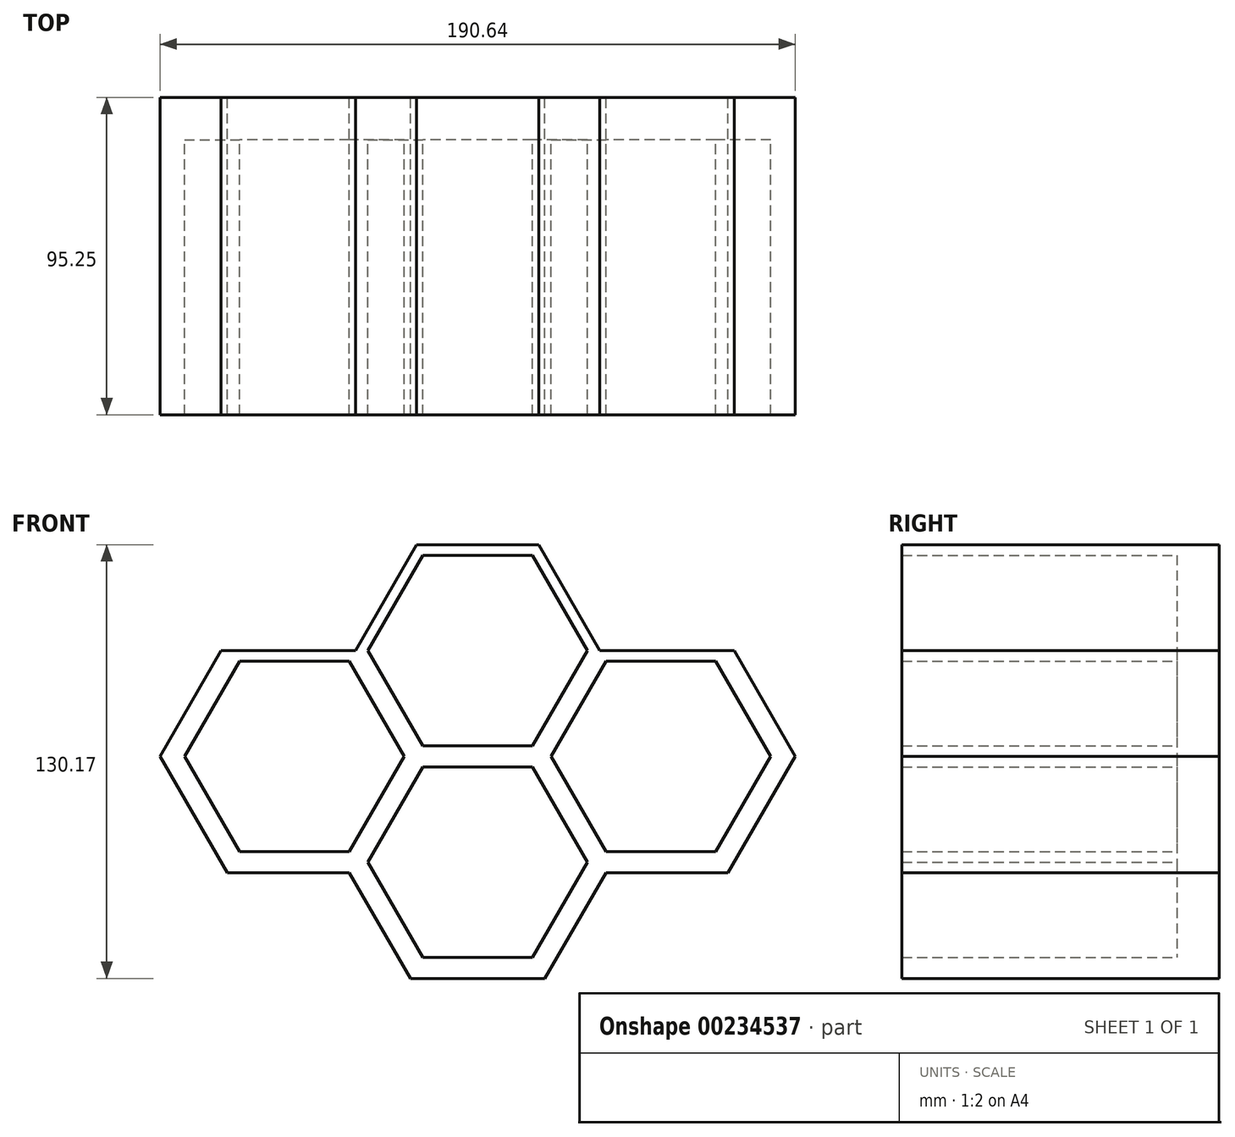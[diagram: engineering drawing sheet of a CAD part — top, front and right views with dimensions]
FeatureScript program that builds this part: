
annotation { "Feature Type Name" : "Feature", "Feature Type Description" : "" }
export const myFeature = defineFeature(function(context is Context, id is Id, definition is map)
    precondition{}
    {
        {
            var Q0;
            Q0=qCreatedBy(makeId("Front.planeOp"),FACE);
            var sketch = newSketch(context, id + "F0", { "sketchPlane" : qUnion([Q0])});
            skLineSegment(sketch, "E0.3", {"start": v(105.7, 35.04) * mm, "end": v(87.38, 3.3) * mm});
            skLineSegment(sketch, "E0.4", {"start": v(87.38, 3.3) * mm, "end": v(50.71, 3.3) * mm});
            skCircle(sketch, "E1.cCircle", {"center": v(69.05, -28.46) * mm, "radius": 28.57 * mm, "construction": true});
            skLineSegment(sketch, "E1.0", {"start": v(36.05, -28.46) * mm, "end": v(52.55, 0.12) * mm});
            skLineSegment(sketch, "E1.1", {"start": v(52.55, 0.12) * mm, "end": v(85.54, 0.12) * mm});
            skLineSegment(sketch, "E1.2", {"start": v(85.54, 0.12) * mm, "end": v(102.04, -28.46) * mm});
            skLineSegment(sketch, "E1.3", {"start": v(102.04, -28.46) * mm, "end": v(85.54, -57.03) * mm});
            skLineSegment(sketch, "E1.4", {"start": v(85.54, -57.03) * mm, "end": v(52.55, -57.03) * mm});
            skLineSegment(sketch, "E1.5", {"start": v(52.55, -57.03) * mm, "end": v(36.05, -28.46) * mm});
            skPoint(sketch, "E1.0.midPoint", {"position": v(44.3, -14.17) * mm});
            skCircle(sketch, "E2.cCircle", {"center": v(69.05, -28.46) * mm, "radius": 31.75 * mm, "construction": true});
            skLineSegment(sketch, "E2.0", {"start": v(32.38, -28.46) * mm, "end": v(50.71, 3.3) * mm});
            skLineSegment(sketch, "E2.1", {"start": v(50.71, 3.3) * mm, "end": v(87.38, 3.3) * mm});
            skLineSegment(sketch, "E2.2", {"start": v(87.38, 3.3) * mm, "end": v(105.7, -28.46) * mm});
            skLineSegment(sketch, "E2.3", {"start": v(105.7, -28.46) * mm, "end": v(87.38, -60.2) * mm});
            skLineSegment(sketch, "E2.4", {"start": v(87.38, -60.2) * mm, "end": v(50.71, -60.2) * mm});
            skLineSegment(sketch, "E2.5", {"start": v(50.71, -60.2) * mm, "end": v(32.38, -28.46) * mm});
            skPoint(sketch, "E2.0.midPoint", {"position": v(41.55, -12.58) * mm});
            skCircle(sketch, "E3.cCircle", {"center": v(124.04, 3.3) * mm, "radius": 28.58 * mm, "construction": true});
            skLineSegment(sketch, "E3.0", {"start": v(91.04, 3.3) * mm, "end": v(107.54, 31.87) * mm});
            skLineSegment(sketch, "E3.1", {"start": v(107.54, 31.87) * mm, "end": v(140.54, 31.87) * mm});
            skLineSegment(sketch, "E3.2", {"start": v(140.54, 31.87) * mm, "end": v(157.03, 3.3) * mm});
            skLineSegment(sketch, "E3.3", {"start": v(157.03, 3.3) * mm, "end": v(140.54, -25.28) * mm});
            skLineSegment(sketch, "E3.4", {"start": v(140.54, -25.28) * mm, "end": v(107.54, -25.28) * mm});
            skLineSegment(sketch, "E3.5", {"start": v(107.54, -25.28) * mm, "end": v(91.04, 3.3) * mm});
            skPoint(sketch, "E3.0.midPoint", {"position": v(99.3, 17.58) * mm});
            skCircle(sketch, "E4.cCircle", {"center": v(124.04, 3.3) * mm, "radius": 31.75 * mm, "construction": true});
            skLineSegment(sketch, "E4.0", {"start": v(87.38, 3.3) * mm, "end": v(105.7, 35.04) * mm});
            skLineSegment(sketch, "E4.1", {"start": v(105.7, 35.04) * mm, "end": v(142.37, 35.04) * mm});
            skLineSegment(sketch, "E4.2", {"start": v(142.37, 35.04) * mm, "end": v(160.7, 3.3) * mm});
            skLineSegment(sketch, "E4.3", {"start": v(160.7, 3.3) * mm, "end": v(142.37, -28.46) * mm});
            skLineSegment(sketch, "E4.4", {"start": v(142.37, -28.46) * mm, "end": v(105.7, -28.46) * mm});
            skLineSegment(sketch, "E4.5", {"start": v(105.7, -28.46) * mm, "end": v(87.38, 3.3) * mm});
            skPoint(sketch, "E4.0.midPoint", {"position": v(96.54, 19.17) * mm});
            skLineSegment(sketch, "E5.4", {"start": v(142.37, 35.04) * mm, "end": v(105.7, 35.04) * mm});
            skCircle(sketch, "E6.cCircle", {"center": v(124.04, -60.2) * mm, "radius": 28.58 * mm, "construction": true});
            skLineSegment(sketch, "E6.0", {"start": v(91.04, -60.2) * mm, "end": v(107.54, -31.63) * mm});
            skLineSegment(sketch, "E6.1", {"start": v(107.54, -31.63) * mm, "end": v(140.54, -31.63) * mm});
            skLineSegment(sketch, "E6.2", {"start": v(140.54, -31.63) * mm, "end": v(157.03, -60.2) * mm});
            skLineSegment(sketch, "E6.3", {"start": v(157.03, -60.2) * mm, "end": v(140.54, -88.78) * mm});
            skLineSegment(sketch, "E6.4", {"start": v(140.54, -88.78) * mm, "end": v(107.54, -88.78) * mm});
            skLineSegment(sketch, "E6.5", {"start": v(107.54, -88.78) * mm, "end": v(91.04, -60.2) * mm});
            skPoint(sketch, "E6.0.midPoint", {"position": v(99.3, -45.92) * mm});
            skCircle(sketch, "E7.cCircle", {"center": v(124.04, -60.2) * mm, "radius": 31.75 * mm, "construction": true});
            skLineSegment(sketch, "E7.0", {"start": v(87.38, -60.2) * mm, "end": v(105.7, -28.46) * mm});
            skLineSegment(sketch, "E7.1", {"start": v(105.7, -28.46) * mm, "end": v(142.37, -28.46) * mm});
            skLineSegment(sketch, "E7.2", {"start": v(142.37, -28.46) * mm, "end": v(160.7, -60.2) * mm});
            skLineSegment(sketch, "E7.3", {"start": v(160.7, -60.2) * mm, "end": v(142.37, -91.96) * mm});
            skLineSegment(sketch, "E7.4", {"start": v(142.37, -91.96) * mm, "end": v(105.7, -91.96) * mm});
            skLineSegment(sketch, "E7.5", {"start": v(105.7, -91.96) * mm, "end": v(87.38, -60.2) * mm});
            skPoint(sketch, "E7.0.midPoint", {"position": v(96.54, -44.33) * mm});
            skCircle(sketch, "E8.cCircle", {"center": v(179.03, -28.46) * mm, "radius": 28.57 * mm, "construction": true});
            skLineSegment(sketch, "E8.0", {"start": v(146.03, -28.46) * mm, "end": v(162.53, 0.12) * mm});
            skLineSegment(sketch, "E8.1", {"start": v(162.53, 0.12) * mm, "end": v(195.53, 0.12) * mm});
            skLineSegment(sketch, "E8.2", {"start": v(195.53, 0.12) * mm, "end": v(212.03, -28.46) * mm});
            skLineSegment(sketch, "E8.3", {"start": v(212.03, -28.46) * mm, "end": v(195.53, -57.03) * mm});
            skLineSegment(sketch, "E8.4", {"start": v(195.53, -57.03) * mm, "end": v(162.53, -57.03) * mm});
            skLineSegment(sketch, "E8.5", {"start": v(162.53, -57.03) * mm, "end": v(146.03, -28.46) * mm});
            skPoint(sketch, "E8.0.midPoint", {"position": v(154.28, -14.17) * mm});
            skCircle(sketch, "E9.cCircle", {"center": v(179.03, -28.46) * mm, "radius": 31.75 * mm, "construction": true});
            skLineSegment(sketch, "E9.0", {"start": v(142.37, -28.46) * mm, "end": v(160.7, 3.3) * mm});
            skLineSegment(sketch, "E9.1", {"start": v(160.7, 3.3) * mm, "end": v(197.36, 3.3) * mm});
            skLineSegment(sketch, "E9.2", {"start": v(197.36, 3.3) * mm, "end": v(215.7, -28.46) * mm});
            skLineSegment(sketch, "E9.3", {"start": v(215.7, -28.46) * mm, "end": v(197.36, -60.2) * mm});
            skLineSegment(sketch, "E9.4", {"start": v(197.36, -60.2) * mm, "end": v(160.7, -60.2) * mm});
            skLineSegment(sketch, "E9.5", {"start": v(160.7, -60.2) * mm, "end": v(142.37, -28.46) * mm});
            skPoint(sketch, "E9.0.midPoint", {"position": v(151.53, -12.58) * mm});
            skLineSegment(sketch, "E10.4", {"start": v(197.36, 3.3) * mm, "end": v(160.7, 3.3) * mm});
            skLineSegment(sketch, "E10.5", {"start": v(160.7, 3.3) * mm, "end": v(142.37, 35.04) * mm});
            skLineSegment(sketch, "E11", {"start": v(47.05, 3.3) * mm, "end": v(28.72, -28.46) * mm});
            skLineSegment(sketch, "E12", {"start": v(28.72, -28.46) * mm, "end": v(48.88, -63.38) * mm});
            skLineSegment(sketch, "E13", {"start": v(48.88, -63.38) * mm, "end": v(85.54, -63.38) * mm});
            skLineSegment(sketch, "E14", {"start": v(85.54, -63.38) * mm, "end": v(103.87, -95.13) * mm});
            skLineSegment(sketch, "E15", {"start": v(103.87, -95.13) * mm, "end": v(144.2, -95.13) * mm});
            skLineSegment(sketch, "E16", {"start": v(144.2, -95.13) * mm, "end": v(162.53, -63.38) * mm});
            skLineSegment(sketch, "E17", {"start": v(162.53, -63.38) * mm, "end": v(199.2, -63.38) * mm});
            skLineSegment(sketch, "E18", {"start": v(199.2, -63.38) * mm, "end": v(219.36, -28.46) * mm});
            skLineSegment(sketch, "E19", {"start": v(219.36, -28.46) * mm, "end": v(201.03, 3.3) * mm});
            skLineSegment(sketch, "E20", {"start": v(50.71, 3.3) * mm, "end": v(47.05, 3.3) * mm});
            skLineSegment(sketch, "E21", {"start": v(201.03, 3.3) * mm, "end": v(197.36, 3.3) * mm});
            skSolve(sketch);
        }
        {
            var Q0;
            Q0=makeQuery(id+"F0.imprint","IMPRINT",FACE,{"disambiguationData":[TD([[makeQuery(id+"F0.imprint","IMPRINT",EDGE,{"derivedFrom":sQuery(id+"F0.wireOp",EDGE,"68d16a58-0471-4e1c-b2b3-2a61df7c0d9d.0")}),-1.0]])]});
            var Q1;
            Q1=makeQuery(id+"F0.imprint","IMPRINT",FACE,{"disambiguationData":[TD([[makeQuery(id+"F0.imprint","IMPRINT",EDGE,{"derivedFrom":sQuery(id+"F0.wireOp",EDGE,"E8.0")}),-1.0]])]});
            var Q2;
            Q2=makeQuery(id+"F0.imprint","IMPRINT",FACE,{"disambiguationData":[TD([[makeQuery(id+"F0.imprint","IMPRINT",EDGE,{"derivedFrom":sQuery(id+"F0.wireOp",EDGE,"cad1e4f3-bd43-45ec-b31a-1d5006939c94.0")}),-1.0]])]});
            var Q3;
            Q3=makeQuery(id+"F0.imprint","IMPRINT",FACE,{"disambiguationData":[TD([[makeQuery(id+"F0.imprint","IMPRINT",EDGE,{"derivedFrom":sQuery(id+"F0.wireOp",EDGE,"b43d4d8c-f78a-4ff8-8565-99a66ce6ec5f.0")}),-1.0]])]});
            var Q4;
            Q4=makeQuery(id+"F0.imprint","IMPRINT",FACE,{"disambiguationData":[TD([[makeQuery(id+"F0.imprint","IMPRINT",EDGE,{"derivedFrom":sQuery(id+"F0.wireOp",EDGE,"8c75d941-d110-4871-aa41-90a72d60fb2b.0")}),-1.0]])]});
            var Q5;
            Q5=makeQuery(id+"F0.imprint","IMPRINT",FACE,{"disambiguationData":[TD([[makeQuery(id+"F0.imprint","IMPRINT",EDGE,{"derivedFrom":sQuery(id+"F0.wireOp",EDGE,"258573fa-3544-418e-8bc5-5d37e5b8ba09.0")}),-1.0]])]});
            var Q6;
            Q6=makeQuery(id+"F0.imprint","IMPRINT",FACE,{"disambiguationData":[TD([[makeQuery(id+"F0.imprint","IMPRINT",EDGE,{"derivedFrom":sQuery(id+"F0.wireOp",EDGE,"0bf0733b-7d93-4c2e-8366-56d2cde24658.0")}),-1.0]])]});
            var Q7;
            Q7=makeQuery(id+"F0.imprint","IMPRINT",FACE,{"disambiguationData":[TD([[makeQuery(id+"F0.imprint","IMPRINT",EDGE,{"derivedFrom":sQuery(id+"F0.wireOp",EDGE,"93717492-86db-456f-ae55-f71e4e93837b.0")}),-1.0]])]});
            var Q8;
            Q8=makeQuery(id+"F0.imprint","IMPRINT",FACE,{"disambiguationData":[TD([[makeQuery(id+"F0.imprint","IMPRINT",EDGE,{"derivedFrom":sQuery(id+"F0.wireOp",EDGE,"f16ea8c9-6b67-4651-8441-f7eb3c0ce7d7.0")}),-1.0]])]});
            var Q9;
            Q9=makeQuery(id+"F0.imprint","IMPRINT",FACE,{"disambiguationData":[TD([[makeQuery(id+"F0.imprint","IMPRINT",EDGE,{"derivedFrom":sQuery(id+"F0.wireOp",EDGE,"0306a0a6-7289-4661-a415-5fa5585f2cb5.0")}),-1.0]])]});
            var Q10;
            Q10=makeQuery(id+"F0.imprint","IMPRINT",FACE,{"disambiguationData":[TD([[makeQuery(id+"F0.imprint","IMPRINT",EDGE,{"derivedFrom":sQuery(id+"F0.wireOp",EDGE,"0a91a14e-ea0c-483f-91eb-c48bd73cb0e6.0")}),-1.0]])]});
            var Q11;
            Q11=makeQuery(id+"F0.imprint","IMPRINT",FACE,{"disambiguationData":[TD([[makeQuery(id+"F0.imprint","IMPRINT",EDGE,{"derivedFrom":sQuery(id+"F0.wireOp",EDGE,"cbfd9497-f7fe-4f18-9288-d90aa8075d81.0")}),-1.0]])]});
            var Q12;
            Q12=makeQuery(id+"F0.imprint","IMPRINT",FACE,{"disambiguationData":[TD([[makeQuery(id+"F0.imprint","IMPRINT",EDGE,{"derivedFrom":sQuery(id+"F0.wireOp",EDGE,"6282d196-dd8f-4bb0-bca4-b9108e277473.0")}),-1.0]])]});
            var Q13;
            Q13=makeQuery(id+"F0.imprint","IMPRINT",FACE,{"disambiguationData":[TD([[makeQuery(id+"F0.imprint","IMPRINT",EDGE,{"derivedFrom":sQuery(id+"F0.wireOp",EDGE,"084ca30c-4dc0-463f-bfd9-557787ed9a2f.0")}),-1.0]])]});
            var Q14;
            Q14=makeQuery(id+"F0.imprint","IMPRINT",FACE,{"disambiguationData":[TD([[makeQuery(id+"F0.imprint","IMPRINT",EDGE,{"derivedFrom":sQuery(id+"F0.wireOp",EDGE,"06c29831-6b25-410b-9247-4ee044b7735c.0")}),-1.0]])]});
            var Q15;
            Q15=makeQuery(id+"F0.imprint","IMPRINT",FACE,{"disambiguationData":[TD([[makeQuery(id+"F0.imprint","IMPRINT",EDGE,{"derivedFrom":sQuery(id+"F0.wireOp",EDGE,"b8eec94e-d97e-439b-aaac-63499233db4c.0")}),-1.0]])]});
            var Q16;
            Q16=makeQuery(id+"F0.imprint","IMPRINT",FACE,{"disambiguationData":[TD([[makeQuery(id+"F0.imprint","IMPRINT",EDGE,{"derivedFrom":sQuery(id+"F0.wireOp",EDGE,"E1.0")}),-1.0]])]});
            var Q17;
            Q17=makeQuery(id+"F0.imprint","IMPRINT",FACE,{"disambiguationData":[TD([[makeQuery(id+"F0.imprint","IMPRINT",EDGE,{"derivedFrom":sQuery(id+"F0.wireOp",EDGE,"E3.0")}),-1.0]])]});
            var Q18;
            Q18=makeQuery(id+"F0.imprint","IMPRINT",FACE,{"disambiguationData":[TD([[makeQuery(id+"F0.imprint","IMPRINT",EDGE,{"derivedFrom":sQuery(id+"F0.wireOp",EDGE,"a1daa6ae-7864-4614-8fb9-3511dddc1266.0")}),-1.0]])]});
            var Q19;
            Q19=makeQuery(id+"F0.imprint","IMPRINT",FACE,{"disambiguationData":[TD([[makeQuery(id+"F0.imprint","IMPRINT",EDGE,{"derivedFrom":sQuery(id+"F0.wireOp",EDGE,"37efd634-c264-4683-8864-08b38c7986ca.0")}),-1.0]])]});
            var Q20;
            Q20=makeQuery(id+"F0.imprint","IMPRINT",FACE,{"disambiguationData":[TD([[makeQuery(id+"F0.imprint","IMPRINT",EDGE,{"derivedFrom":sQuery(id+"F0.wireOp",EDGE,"f2dd3995-374a-43c5-8725-4a87181dc8c5.0")}),-1.0]])]});
            var Q21;
            Q21=makeQuery(id+"F0.imprint","IMPRINT",FACE,{"disambiguationData":[TD([[makeQuery(id+"F0.imprint","IMPRINT",EDGE,{"derivedFrom":sQuery(id+"F0.wireOp",EDGE,"1f2aec04-a318-49b9-a42e-ea2fce35ed6c.0")}),-1.0]])]});
            var Q22;
            Q22=makeQuery(id+"F0.imprint","IMPRINT",FACE,{"disambiguationData":[TD([[makeQuery(id+"F0.imprint","IMPRINT",EDGE,{"derivedFrom":sQuery(id+"F0.wireOp",EDGE,"E6.0")}),-1.0]])]});
            var Q23;
            Q23=makeQuery(id+"F0.imprint","IMPRINT",FACE,{"disambiguationData":[TD([[makeQuery(id+"F0.imprint","IMPRINT",EDGE,{"derivedFrom":sQuery(id+"F0.wireOp",EDGE,"4e92e904-9607-490d-a429-b319c41500d9.0")}),-1.0]])]});
            var Q24;
            Q24=makeQuery(id+"F0.imprint","IMPRINT",FACE,{"disambiguationData":[TD([[makeQuery(id+"F0.imprint","IMPRINT",EDGE,{"derivedFrom":sQuery(id+"F0.wireOp",EDGE,"084ca30c-4dc0-463f-bfd9-557787ed9a2f.0")}),1.0]])]});
            var Q25;
            Q25=makeQuery(id+"F0.imprint","IMPRINT",FACE,{"disambiguationData":[TD([[makeQuery(id+"F0.imprint","IMPRINT",EDGE,{"derivedFrom":sQuery(id+"F0.wireOp",EDGE,"1f2aec04-a318-49b9-a42e-ea2fce35ed6c.0")}),1.0]])]});
            var Q26;
            Q26=makeQuery(id+"F0.imprint","IMPRINT",FACE,{"disambiguationData":[TD([[makeQuery(id+"F0.imprint","IMPRINT",EDGE,{"derivedFrom":sQuery(id+"F0.wireOp",EDGE,"E3.0")}),1.0]])]});
            var Q27;
            Q27=makeQuery(id+"F0.imprint","IMPRINT",FACE,{"disambiguationData":[TD([[makeQuery(id+"F0.imprint","IMPRINT",EDGE,{"derivedFrom":sQuery(id+"F0.wireOp",EDGE,"E1.0")}),1.0]])]});
            var Q28;
            Q28=makeQuery(id+"F0.imprint","IMPRINT",FACE,{"disambiguationData":[TD([[makeQuery(id+"F0.imprint","IMPRINT",EDGE,{"derivedFrom":sQuery(id+"F0.wireOp",EDGE,"4e92e904-9607-490d-a429-b319c41500d9.0")}),1.0]])]});
            var Q29;
            Q29=makeQuery(id+"F0.imprint","IMPRINT",FACE,{"disambiguationData":[TD([[makeQuery(id+"F0.imprint","IMPRINT",EDGE,{"derivedFrom":sQuery(id+"F0.wireOp",EDGE,"b43d4d8c-f78a-4ff8-8565-99a66ce6ec5f.0")}),1.0]])]});
            var Q30;
            Q30=makeQuery(id+"F0.imprint","IMPRINT",FACE,{"disambiguationData":[TD([[makeQuery(id+"F0.imprint","IMPRINT",EDGE,{"derivedFrom":sQuery(id+"F0.wireOp",EDGE,"E8.0")}),1.0]])]});
            var Q31;
            Q31=makeQuery(id+"F0.imprint","IMPRINT",FACE,{"disambiguationData":[TD([[makeQuery(id+"F0.imprint","IMPRINT",EDGE,{"derivedFrom":sQuery(id+"F0.wireOp",EDGE,"0a91a14e-ea0c-483f-91eb-c48bd73cb0e6.0")}),1.0]])]});
            var Q32;
            Q32=makeQuery(id+"F0.imprint","IMPRINT",FACE,{"disambiguationData":[TD([[makeQuery(id+"F0.imprint","IMPRINT",EDGE,{"derivedFrom":sQuery(id+"F0.wireOp",EDGE,"258573fa-3544-418e-8bc5-5d37e5b8ba09.0")}),1.0]])]});
            var Q33;
            Q33=makeQuery(id+"F0.imprint","IMPRINT",FACE,{"disambiguationData":[TD([[makeQuery(id+"F0.imprint","IMPRINT",EDGE,{"derivedFrom":sQuery(id+"F0.wireOp",EDGE,"cbfd9497-f7fe-4f18-9288-d90aa8075d81.0")}),1.0]])]});
            var Q34;
            Q34=makeQuery(id+"F0.imprint","IMPRINT",FACE,{"disambiguationData":[TD([[makeQuery(id+"F0.imprint","IMPRINT",EDGE,{"derivedFrom":sQuery(id+"F0.wireOp",EDGE,"E6.0")}),1.0]])]});
            var Q35;
            Q35=makeQuery(id+"F0.imprint","IMPRINT",FACE,{"disambiguationData":[TD([[makeQuery(id+"F0.imprint","IMPRINT",EDGE,{"derivedFrom":sQuery(id+"F0.wireOp",EDGE,"b8eec94e-d97e-439b-aaac-63499233db4c.0")}),1.0]])]});
            var Q36;
            Q36=makeQuery(id+"F0.imprint","IMPRINT",FACE,{"disambiguationData":[TD([[makeQuery(id+"F0.imprint","IMPRINT",EDGE,{"derivedFrom":sQuery(id+"F0.wireOp",EDGE,"8c75d941-d110-4871-aa41-90a72d60fb2b.0")}),1.0]])]});
            var Q37;
            Q37=makeQuery(id+"F0.imprint","IMPRINT",FACE,{"disambiguationData":[TD([[makeQuery(id+"F0.imprint","IMPRINT",EDGE,{"derivedFrom":sQuery(id+"F0.wireOp",EDGE,"f16ea8c9-6b67-4651-8441-f7eb3c0ce7d7.0")}),1.0]])]});
            var Q38;
            Q38=makeQuery(id+"F0.imprint","IMPRINT",FACE,{"disambiguationData":[TD([[makeQuery(id+"F0.imprint","IMPRINT",EDGE,{"derivedFrom":sQuery(id+"F0.wireOp",EDGE,"37efd634-c264-4683-8864-08b38c7986ca.0")}),1.0]])]});
            var Q39;
            Q39=makeQuery(id+"F0.imprint","IMPRINT",FACE,{"disambiguationData":[TD([[makeQuery(id+"F0.imprint","IMPRINT",EDGE,{"derivedFrom":sQuery(id+"F0.wireOp",EDGE,"68d16a58-0471-4e1c-b2b3-2a61df7c0d9d.0")}),1.0]])]});
            var Q40;
            Q40=makeQuery(id+"F0.imprint","IMPRINT",FACE,{"disambiguationData":[TD([[makeQuery(id+"F0.imprint","IMPRINT",EDGE,{"derivedFrom":sQuery(id+"F0.wireOp",EDGE,"0306a0a6-7289-4661-a415-5fa5585f2cb5.0")}),1.0]])]});
            var Q41;
            Q41=makeQuery(id+"F0.imprint","IMPRINT",FACE,{"disambiguationData":[TD([[makeQuery(id+"F0.imprint","IMPRINT",EDGE,{"derivedFrom":sQuery(id+"F0.wireOp",EDGE,"0bf0733b-7d93-4c2e-8366-56d2cde24658.0")}),1.0]])]});
            var Q42;
            Q42=makeQuery(id+"F0.imprint","IMPRINT",FACE,{"disambiguationData":[TD([[makeQuery(id+"F0.imprint","IMPRINT",EDGE,{"derivedFrom":sQuery(id+"F0.wireOp",EDGE,"06c29831-6b25-410b-9247-4ee044b7735c.0")}),1.0]])]});
            var Q43;
            Q43=makeQuery(id+"F0.imprint","IMPRINT",FACE,{"disambiguationData":[TD([[makeQuery(id+"F0.imprint","IMPRINT",EDGE,{"derivedFrom":sQuery(id+"F0.wireOp",EDGE,"6282d196-dd8f-4bb0-bca4-b9108e277473.0")}),1.0]])]});
            var Q44;
            Q44=makeQuery(id+"F0.imprint","IMPRINT",FACE,{"disambiguationData":[TD([[makeQuery(id+"F0.imprint","IMPRINT",EDGE,{"derivedFrom":sQuery(id+"F0.wireOp",EDGE,"cad1e4f3-bd43-45ec-b31a-1d5006939c94.0")}),1.0]])]});
            var Q45;
            Q45=makeQuery(id+"F0.imprint","IMPRINT",FACE,{"disambiguationData":[TD([[makeQuery(id+"F0.imprint","IMPRINT",EDGE,{"derivedFrom":sQuery(id+"F0.wireOp",EDGE,"f2dd3995-374a-43c5-8725-4a87181dc8c5.0")}),1.0]])]});
            var Q46;
            Q46=makeQuery(id+"F0.imprint","IMPRINT",FACE,{"disambiguationData":[TD([[makeQuery(id+"F0.imprint","IMPRINT",EDGE,{"derivedFrom":sQuery(id+"F0.wireOp",EDGE,"a1daa6ae-7864-4614-8fb9-3511dddc1266.0")}),1.0]])]});
            var Q47;
            Q47=makeQuery(id+"F0.imprint","IMPRINT",FACE,{"disambiguationData":[TD([[makeQuery(id+"F0.imprint","IMPRINT",EDGE,{"derivedFrom":sQuery(id+"F0.wireOp",EDGE,"93717492-86db-456f-ae55-f71e4e93837b.0")}),1.0]])]});
            extrude(context, id + "F1", {"entities" : qUnion([Q0, Q1, Q2, Q3, Q4, Q5, Q6, Q7, Q8, Q9, Q10, Q11, Q12, Q13, Q14, Q15, Q16, Q17, Q18, Q19, Q20, Q21, Q22, Q23, Q24, Q25, Q26, Q27, Q28, Q29, Q30, Q31, Q32, Q33, Q34, Q35, Q36, Q37, Q38, Q39, Q40, Q41, Q42, Q43, Q44, Q45, Q46, Q47]), "depth" : 12.7 * mm});
        }
        {
            var Q0;
            Q0=makeQuery(id+"F0.imprint","IMPRINT",FACE,{"disambiguationData":[TD([[makeQuery(id+"F0.imprint","IMPRINT",EDGE,{"derivedFrom":sQuery(id+"F0.wireOp",EDGE,"8c75d941-d110-4871-aa41-90a72d60fb2b.0")}),1.0]])]});
            var Q1;
            Q1=makeQuery(id+"F0.imprint","IMPRINT",FACE,{"disambiguationData":[TD([[makeQuery(id+"F0.imprint","IMPRINT",EDGE,{"derivedFrom":sQuery(id+"F0.wireOp",EDGE,"b8eec94e-d97e-439b-aaac-63499233db4c.0")}),1.0]])]});
            var Q2;
            Q2=makeQuery(id+"F0.imprint","IMPRINT",FACE,{"disambiguationData":[TD([[makeQuery(id+"F0.imprint","IMPRINT",EDGE,{"derivedFrom":sQuery(id+"F0.wireOp",EDGE,"cad1e4f3-bd43-45ec-b31a-1d5006939c94.0")}),1.0]])]});
            var Q3;
            Q3=makeQuery(id+"F0.imprint","IMPRINT",FACE,{"disambiguationData":[TD([[makeQuery(id+"F0.imprint","IMPRINT",EDGE,{"derivedFrom":sQuery(id+"F0.wireOp",EDGE,"68d16a58-0471-4e1c-b2b3-2a61df7c0d9d.0")}),1.0]])]});
            var Q4;
            Q4=makeQuery(id+"F0.imprint","IMPRINT",FACE,{"disambiguationData":[TD([[makeQuery(id+"F0.imprint","IMPRINT",EDGE,{"derivedFrom":sQuery(id+"F0.wireOp",EDGE,"0306a0a6-7289-4661-a415-5fa5585f2cb5.0")}),1.0]])]});
            var Q5;
            Q5=makeQuery(id+"F0.imprint","IMPRINT",FACE,{"disambiguationData":[TD([[makeQuery(id+"F0.imprint","IMPRINT",EDGE,{"derivedFrom":sQuery(id+"F0.wireOp",EDGE,"084ca30c-4dc0-463f-bfd9-557787ed9a2f.0")}),1.0]])]});
            var Q6;
            Q6=makeQuery(id+"F0.imprint","IMPRINT",FACE,{"disambiguationData":[TD([[makeQuery(id+"F0.imprint","IMPRINT",EDGE,{"derivedFrom":sQuery(id+"F0.wireOp",EDGE,"4e92e904-9607-490d-a429-b319c41500d9.0")}),1.0]])]});
            var Q7;
            Q7=makeQuery(id+"F0.imprint","IMPRINT",FACE,{"disambiguationData":[TD([[makeQuery(id+"F0.imprint","IMPRINT",EDGE,{"derivedFrom":sQuery(id+"F0.wireOp",EDGE,"a1daa6ae-7864-4614-8fb9-3511dddc1266.0")}),1.0]])]});
            var Q8;
            Q8=makeQuery(id+"F0.imprint","IMPRINT",FACE,{"disambiguationData":[TD([[makeQuery(id+"F0.imprint","IMPRINT",EDGE,{"derivedFrom":sQuery(id+"F0.wireOp",EDGE,"93717492-86db-456f-ae55-f71e4e93837b.0")}),1.0]])]});
            var Q9;
            Q9=makeQuery(id+"F0.imprint","IMPRINT",FACE,{"disambiguationData":[TD([[makeQuery(id+"F0.imprint","IMPRINT",EDGE,{"derivedFrom":sQuery(id+"F0.wireOp",EDGE,"258573fa-3544-418e-8bc5-5d37e5b8ba09.0")}),1.0]])]});
            var Q10;
            Q10=makeQuery(id+"F0.imprint","IMPRINT",FACE,{"disambiguationData":[TD([[makeQuery(id+"F0.imprint","IMPRINT",EDGE,{"derivedFrom":sQuery(id+"F0.wireOp",EDGE,"f2dd3995-374a-43c5-8725-4a87181dc8c5.0")}),1.0]])]});
            var Q11;
            Q11=makeQuery(id+"F0.imprint","IMPRINT",FACE,{"disambiguationData":[TD([[makeQuery(id+"F0.imprint","IMPRINT",EDGE,{"derivedFrom":sQuery(id+"F0.wireOp",EDGE,"E3.0")}),1.0]])]});
            var Q12;
            Q12=makeQuery(id+"F0.imprint","IMPRINT",FACE,{"disambiguationData":[TD([[makeQuery(id+"F0.imprint","IMPRINT",EDGE,{"derivedFrom":sQuery(id+"F0.wireOp",EDGE,"06c29831-6b25-410b-9247-4ee044b7735c.0")}),1.0]])]});
            var Q13;
            Q13=makeQuery(id+"F0.imprint","IMPRINT",FACE,{"disambiguationData":[TD([[makeQuery(id+"F0.imprint","IMPRINT",EDGE,{"derivedFrom":sQuery(id+"F0.wireOp",EDGE,"E8.0")}),1.0]])]});
            var Q14;
            Q14=makeQuery(id+"F0.imprint","IMPRINT",FACE,{"disambiguationData":[TD([[makeQuery(id+"F0.imprint","IMPRINT",EDGE,{"derivedFrom":sQuery(id+"F0.wireOp",EDGE,"E6.0")}),1.0]])]});
            var Q15;
            Q15=makeQuery(id+"F0.imprint","IMPRINT",FACE,{"disambiguationData":[TD([[makeQuery(id+"F0.imprint","IMPRINT",EDGE,{"derivedFrom":sQuery(id+"F0.wireOp",EDGE,"E1.0")}),1.0]])]});
            var Q16;
            Q16=makeQuery(id+"F0.imprint","IMPRINT",FACE,{"disambiguationData":[TD([[makeQuery(id+"F0.imprint","IMPRINT",EDGE,{"derivedFrom":sQuery(id+"F0.wireOp",EDGE,"0a91a14e-ea0c-483f-91eb-c48bd73cb0e6.0")}),1.0]])]});
            var Q17;
            Q17=makeQuery(id+"F0.imprint","IMPRINT",FACE,{"disambiguationData":[TD([[makeQuery(id+"F0.imprint","IMPRINT",EDGE,{"derivedFrom":sQuery(id+"F0.wireOp",EDGE,"37efd634-c264-4683-8864-08b38c7986ca.0")}),1.0]])]});
            var Q18;
            Q18=makeQuery(id+"F0.imprint","IMPRINT",FACE,{"disambiguationData":[TD([[makeQuery(id+"F0.imprint","IMPRINT",EDGE,{"derivedFrom":sQuery(id+"F0.wireOp",EDGE,"cbfd9497-f7fe-4f18-9288-d90aa8075d81.0")}),1.0]])]});
            var Q19;
            Q19=makeQuery(id+"F0.imprint","IMPRINT",FACE,{"disambiguationData":[TD([[makeQuery(id+"F0.imprint","IMPRINT",EDGE,{"derivedFrom":sQuery(id+"F0.wireOp",EDGE,"6282d196-dd8f-4bb0-bca4-b9108e277473.0")}),1.0]])]});
            var Q20;
            Q20=makeQuery(id+"F0.imprint","IMPRINT",FACE,{"disambiguationData":[TD([[makeQuery(id+"F0.imprint","IMPRINT",EDGE,{"derivedFrom":sQuery(id+"F0.wireOp",EDGE,"0bf0733b-7d93-4c2e-8366-56d2cde24658.0")}),1.0]])]});
            var Q21;
            Q21=makeQuery(id+"F0.imprint","IMPRINT",FACE,{"disambiguationData":[TD([[makeQuery(id+"F0.imprint","IMPRINT",EDGE,{"derivedFrom":sQuery(id+"F0.wireOp",EDGE,"b43d4d8c-f78a-4ff8-8565-99a66ce6ec5f.0")}),1.0]])]});
            var Q22;
            Q22=makeQuery(id+"F0.imprint","IMPRINT",FACE,{"disambiguationData":[TD([[makeQuery(id+"F0.imprint","IMPRINT",EDGE,{"derivedFrom":sQuery(id+"F0.wireOp",EDGE,"f16ea8c9-6b67-4651-8441-f7eb3c0ce7d7.0")}),1.0]])]});
            var Q23;
            Q23=makeQuery(id+"F0.imprint","IMPRINT",FACE,{"disambiguationData":[TD([[makeQuery(id+"F0.imprint","IMPRINT",EDGE,{"derivedFrom":sQuery(id+"F0.wireOp",EDGE,"1f2aec04-a318-49b9-a42e-ea2fce35ed6c.0")}),1.0]])]});
            var Q24;
            {var subQ6=sQuery(id+"F0.wireOp",EDGE,"16495d92-3f2e-4778-aa2a-097d1cd616f4.3");Q24=makeQuery(id+"F0.imprint","IMPRINT",FACE,{"disambiguationData":[TD([[makeQuery(id+"F0.imprint","IMPRINT",EDGE,{"derivedFrom":subQ6}),1.0]])]});}
            var Q25;
            Q25=makeQuery(id+"F0.imprint","IMPRINT",FACE,{"disambiguationData":[TD([[makeQuery(id+"F0.imprint","IMPRINT",EDGE,{"derivedFrom":sQuery(id+"F0.wireOp",EDGE,"16495d92-3f2e-4778-aa2a-097d1cd616f4.1")}),1.0]])]});
            var Q26;
            Q26=makeQuery(id+"F0.imprint","IMPRINT",FACE,{"disambiguationData":[TD([[makeQuery(id+"F0.imprint","IMPRINT",EDGE,{"derivedFrom":sQuery(id+"F0.wireOp",EDGE,"E2.0")}),1.0]])]});
            extrude(context, id + "F2", {"entities" : qUnion([Q0, Q1, Q2, Q3, Q4, Q5, Q6, Q7, Q8, Q9, Q10, Q11, Q12, Q13, Q14, Q15, Q16, Q17, Q18, Q19, Q20, Q21, Q22, Q23, Q24, Q25, Q26]), "operationType" : NewBodyOperationType.ADD, "depth" : 95.25 * mm});
        }
    });
